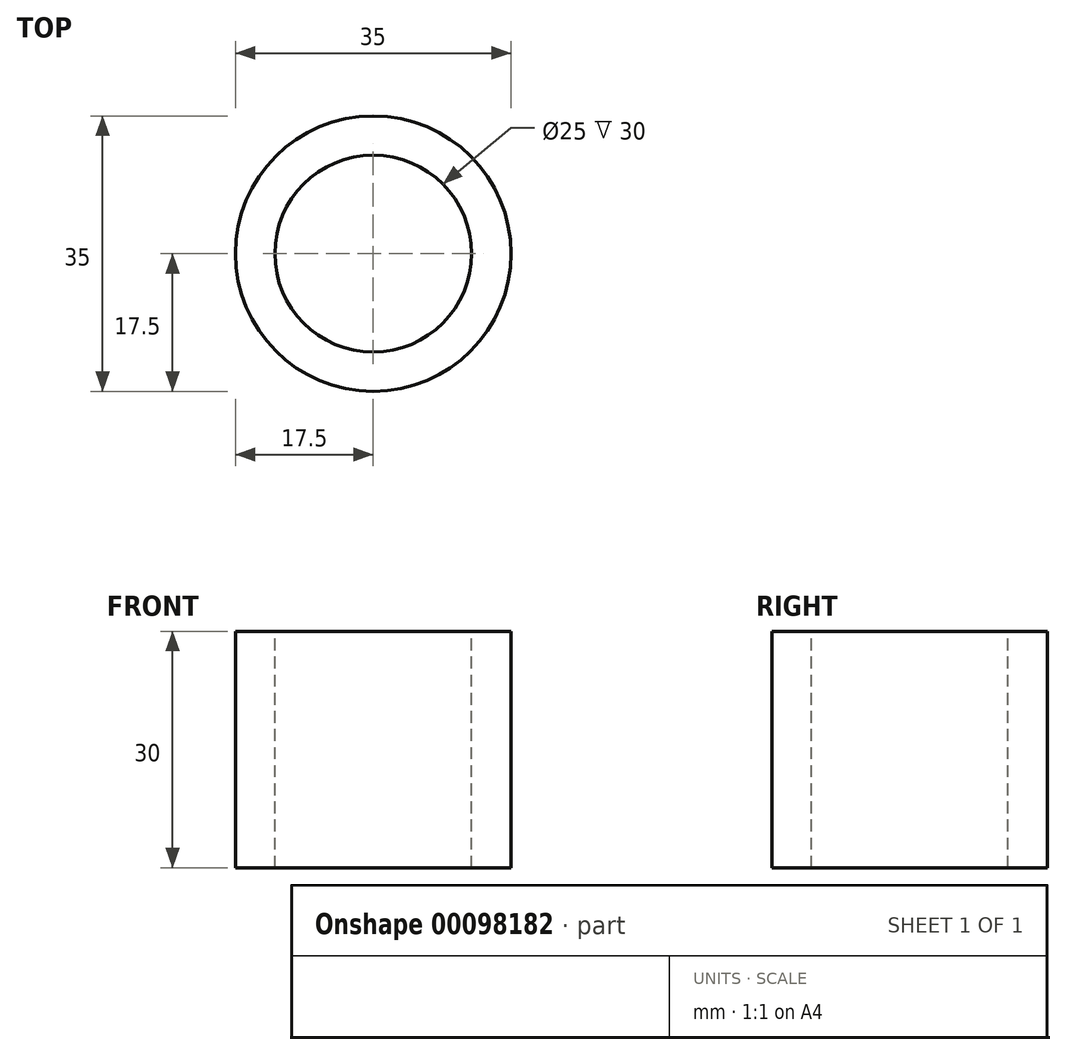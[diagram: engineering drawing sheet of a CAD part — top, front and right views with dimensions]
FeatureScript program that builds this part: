
annotation { "Feature Type Name" : "Feature", "Feature Type Description" : "" }
export const myFeature = defineFeature(function(context is Context, id is Id, definition is map)
    precondition{}
    {
        {
            var Q0;
            Q0=qCreatedBy(makeId("Top.planeOp"),FACE);
            var sketch = newSketch(context, id + "F0", { "sketchPlane" : qUnion([Q0])});
            skCircle(sketch, "E0", {"center": v(0, 0) * mm, "radius": 12.5 * mm});
            skCircle(sketch, "E1", {"center": v(0, 0) * mm, "radius": 17.5 * mm});
            skSolve(sketch);
        }
        {
            var Q0;
            Q0=makeQuery(id+"F0.imprint","IMPRINT",FACE,{"disambiguationData":[TD([[makeQuery(id+"F0.imprint","IMPRINT",EDGE,{"derivedFrom":sQuery(id+"F0.wireOp",EDGE,"E0")}),-1.0]])]});
            extrude(context, id + "F1", {"entities" : qUnion([Q0]), "oppositeDirection" : true, "depth" : 30 * mm});
        }
    });
